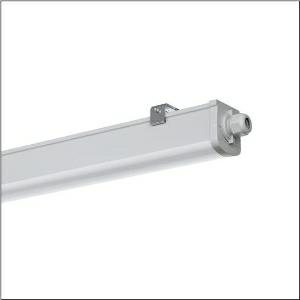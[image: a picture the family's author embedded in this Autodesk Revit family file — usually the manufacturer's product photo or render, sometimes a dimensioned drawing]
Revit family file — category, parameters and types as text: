
# Revit family: monsun_r__31_51fa20dk430b_aae0
name_source: partatom
category: Lighting Fixtures
units: mm (PartAtom-declared; Revit-internal decimal feet)

## family parameters
Cut with Voids When Loaded = No
Host = Face
Light Source = No
Part Type = Normal
Room Calculation Point = No
Round Connector Dimension = Use Diameter
Shared = No

## types (1)
- Monsun® 31 (1 x LED, 3000 lm, 22 W, 4000K)
    Apparent Load = 22 VA
    CIE Flux Codes = 42 72 91 92 100
    Color Rendering = 80
    Color Temperature = 4000K
    Default Elevation = 1800 mm
    Description = Monsun® 31, damp-proof luminaire, primary optical cover: diffuser, of PC, frosted, light emission: direct distribution, primary light characteristic: symmetric, installation type: surface-mounted, LED, rated luminous flux: 3.000lm, luminous efficacy: 136lm/W, light colour: 840, colour temperature: 4000K, control gear: ECG, with terminal, 5+1-pole, max. 2.5mm², through-wiring: 3x 2.5mm² + 3x 1.5mm², mains connection: 220..240V, AC, 50/60Hz, rated input power: 22W, housing, luminaire housing, of PC, light grey (RAL 7035), length: 1.158mm, width: 68mm, height: 76mm, protection rating (complete): IP66, insulation class (complete): insulation class II (safety insulation), certification: CE, ENEC, UKCA, protection symbol: D, impact resistance: IK08, permissible operating ambient temperature: -20..+40°C, corresponds to IFS (International Featured Standards) requirements for safety and quality in the food industry, packaging unit: 1 piece
    Height = 77 mm
    Lamp = 1 x LED
    Lamp Light Flux = 3000 lm
    Lamp Power = 22 W
    Lamp count = 1
    Length = 1218 mm
    Luminous efficacy = 136 lm/W
    Manufacturer = Siteco
    ModVariant = No
    Model = 51FA20DK430B
    Mounting Place = Ceiling
    Mounting Type = Surface mounted
    Number of Poles = 1
    OnlyDefault = Yes
    Power Factor = 1
    Product Name = Monsun® 31
    Product group = damp-proof luminaire | ceiling mounted
    ProductGroupID = 300
    Protection Class = Protection class II
    Protection Degree = IP 66
    RLX_Detail_Level = 1
    RlxData = <blob elided: 32725 chars, md5=583f3401>
    Socket = socket
    Standby Power = 0 W
    System Light Flux = 3000 lm
    System Power = 22 W
    Type Comments = Product without accessories
    Type Image = l_1006174.jpg
    URL = http://relux.com
    VarID = ---
    Voltage = 0 V
    Weight = 0.00 kg
    Width = 69 mm

## geometry (parser evidence)
native form markers: Blend x4, Sweep x13
no freeform markers — native parametric forms only
